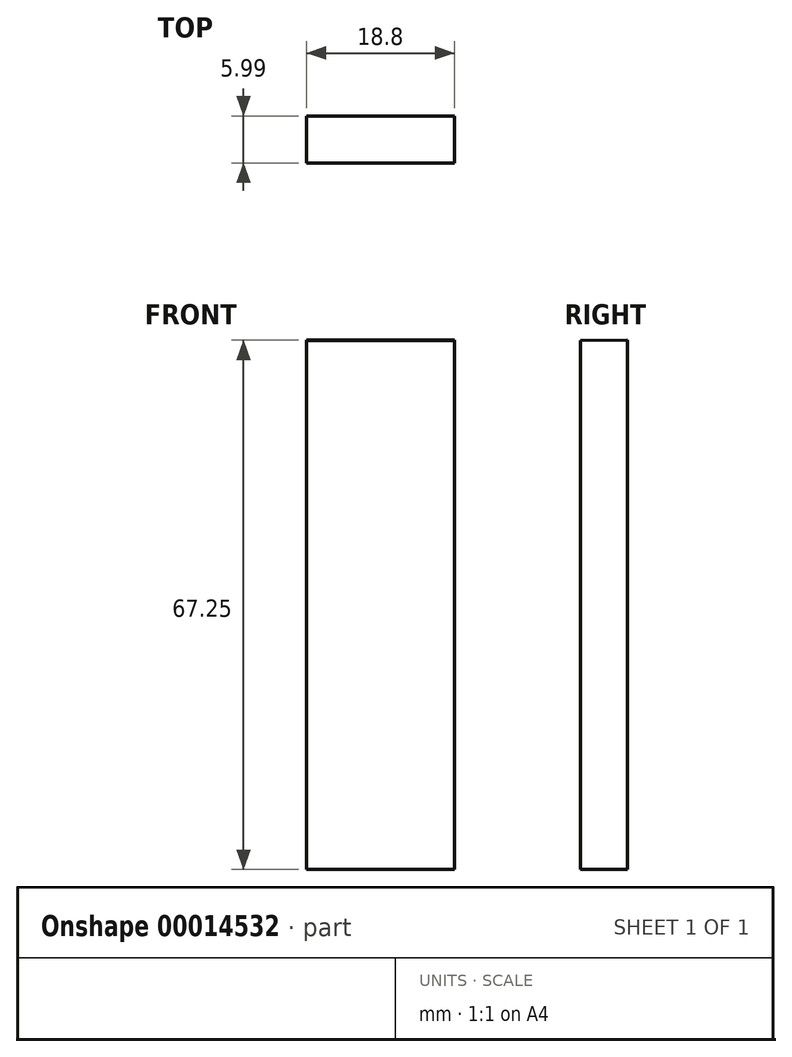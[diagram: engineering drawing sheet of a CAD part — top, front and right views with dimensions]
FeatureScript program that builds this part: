
annotation { "Feature Type Name" : "Feature", "Feature Type Description" : "" }
export const myFeature = defineFeature(function(context is Context, id is Id, definition is map)
    precondition{}
    {
        {
            var Q0;
            Q0=qCreatedBy(makeId("Right.planeOp"),FACE);
            var sketch = newSketch(context, id + "F0", { "sketchPlane" : qUnion([Q0])});
            skLineSegment(sketch, "E0", {"start": v(-36.65, 75.1) * mm, "end": v(-36.65, 7.92) * mm});
            skLineSegment(sketch, "E1", {"start": v(-36.65, 7.92) * mm, "end": v(-30.66, 7.92) * mm});
            skLineSegment(sketch, "E2", {"start": v(-30.66, 7.92) * mm, "end": v(-30.66, 75.17) * mm});
            skLineSegment(sketch, "E3", {"start": v(-30.66, 75.17) * mm, "end": v(-36.65, 75.1) * mm});
            skSolve(sketch);
        }
        {
            var Q0;
            Q0 = qSketchRegion(id + "F0", true);
            extrude(context, id + "F1", {"entities" : qUnion([Q0]), "depth" : 18.8 * mm});
        }
    });
